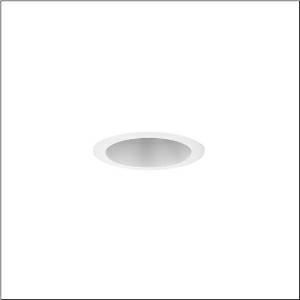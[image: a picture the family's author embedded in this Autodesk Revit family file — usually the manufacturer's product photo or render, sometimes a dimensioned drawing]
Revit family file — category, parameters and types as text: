
# Revit family: lunis_31-l_51dn16me31b
name_source: partatom
category: Lighting Fixtures
units: mm (PartAtom-declared; Revit-internal decimal feet)

## family parameters
Cut with Voids When Loaded = No
Host = Face
Light Source = No
Part Type = Normal
Room Calculation Point = No
Round Connector Dimension = Use Diameter
Shared = No

## types (1)
- --- (1 x LED, 1600 lm, 11.5 W, 3000K)
    Apparent Load = 12 VA
    CIE Flux Codes = 76 93 99 100 100
    Color Rendering = 80
    Color Temperature = 3000K
    Default Elevation = 1800 mm
    Description = Lunis 31, -L, downlight, light control with reflector, light emission: direct distribution, LED rated luminous flux: 1.600lm, light colour: 830, mains connection: 220..240V, AC, 50/60Hz, housing, of aluminium, white, protection rating (complete): IP20, protection rating (on room side): IP54, insulation class (complete): insulation class II (safety insulation), certification: CE, packaging unit: 1 piece
    Height = 0 mm  [stored 0 ft]
    Lamp = 1 x LED
    Lamp Light Flux = 1600 lm
    Lamp Power = 11.5 W
    Lamp count = 1
    Length = 188 mm  [stored 0.616798 ft]
    Luminous efficacy = 139 lm/W
    Manufacturer = Siteco
    ModVariant = No
    Model = 51DN16ME31B
    Mounting Place = Ceiling
    Mounting Type = Recessed
    Number of Poles = 1
    OnlyDefault = Yes
    Power Factor = 1
    Product Name = Lunis 31-L
    Product group = downlight
    ProductGroupID = 400
    Protection Class = Protection class II
    Protection Degree = IP 20
    RLX_Detail_Level = 1
    RLX_Emergency_Light_Flux = 0 lm
    RLX_Emergency_Type = 0
    RLX_Emergency_Type_DB = No
    RlxData = <blob elided: 22485 chars, md5=912e2a0d>
    Socket = socket
    Standby Power = 0 W
    System Light Flux = 1600 lm
    System Power = 12 W
    Type Comments = individual setting: luminous flux: 100 % | (OFF | ON) | 300 mA
    Type Image = l_1345911.jpg
    URL = http://relux.com
    VarID = @adj_010149
    Voltage = 0 V
    Weight = 0.00 kg
    Width = 0 mm  [stored 0 ft]

note: [stored X ft] marks values corroborated as IEEE doubles in the binary element streams (Revit-internal decimal feet)

## geometry (parser evidence)
native form markers: Blend x4, Sweep x10
no freeform markers — native parametric forms only
